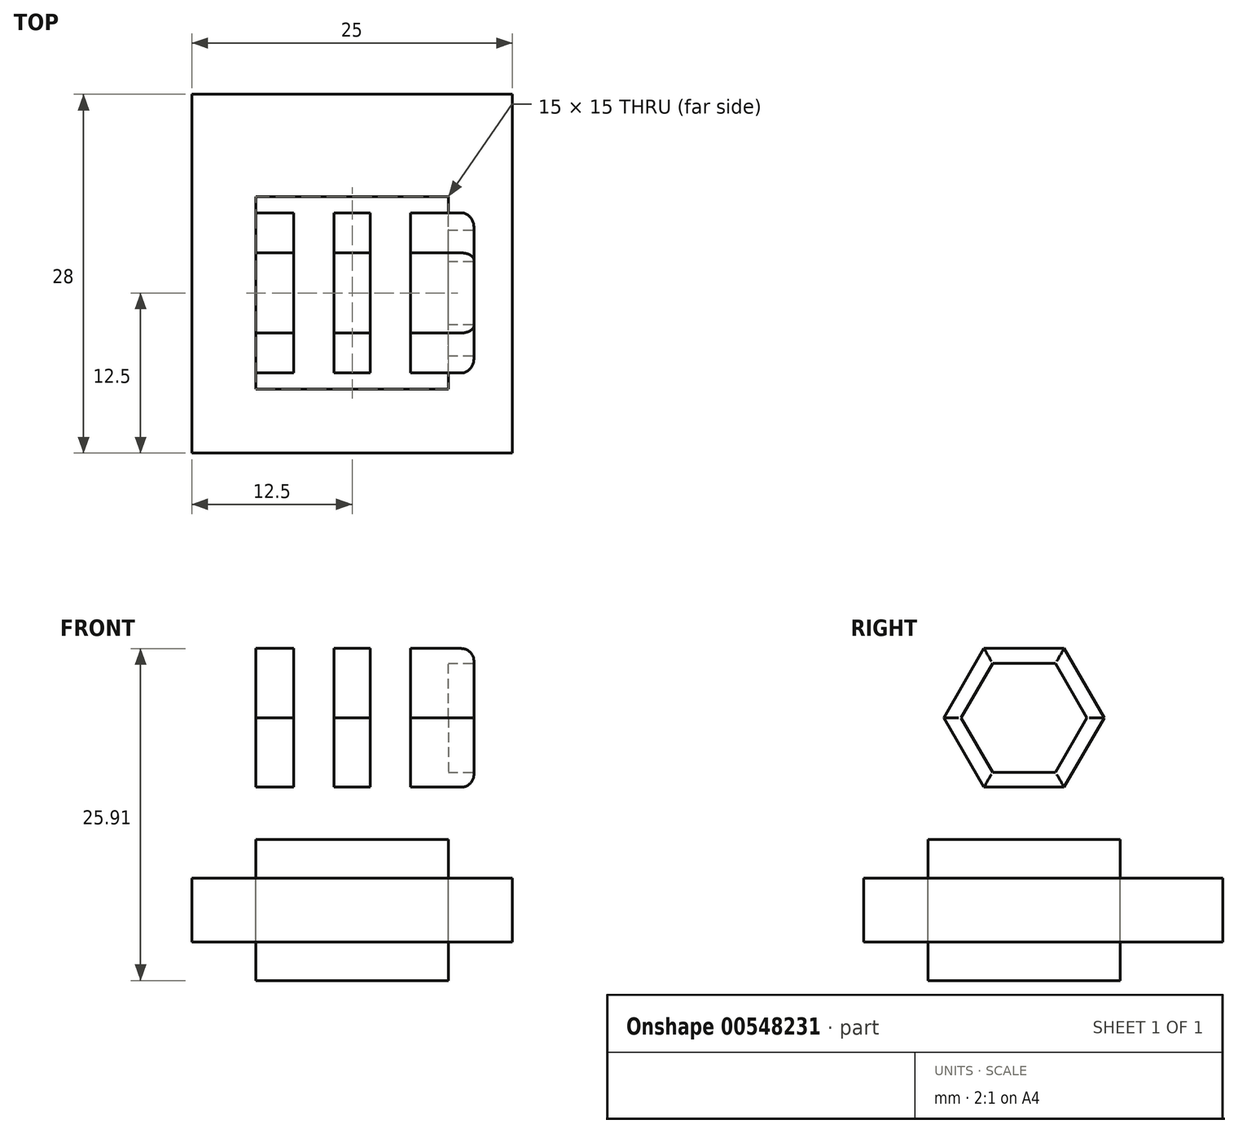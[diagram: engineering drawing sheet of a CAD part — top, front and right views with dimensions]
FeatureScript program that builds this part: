
annotation { "Feature Type Name" : "Feature", "Feature Type Description" : "" }
export const myFeature = defineFeature(function(context is Context, id is Id, definition is map)
    precondition{}
    {
        {
            var Q0;
            Q0=qCreatedBy(makeId("Right.planeOp"),FACE);
            var sketch = newSketch(context, id + "F0", { "sketchPlane" : qUnion([Q0])});
            skPoint(sketch, "E0", {"position": v(0, 12.5) * mm});
            skPoint(sketch, "E1", {"position": v(7.5, 0) * mm});
            skPoint(sketch, "E2.end.orphan", {"position": v(-7.5, 0) * mm});
            skLineSegment(sketch, "E3.top", {"start": v(-7.5, 0) * mm, "end": v(7.5, 0) * mm});
            skLineSegment(sketch, "E3.left", {"start": v(-7.5, 12.5) * mm, "end": v(-7.5, 0) * mm});
            skLineSegment(sketch, "E3.right", {"start": v(7.5, 12.5) * mm, "end": v(7.5, 0) * mm});
            skArc(sketch, "E4", {"start": v(7.5, 12.5) * mm, "mid": v(0, 20) * mm, "end": v(-7.5, 12.5) * mm});
            skCircle(sketch, "E5.cCircle", {"center": v(0, 12.5) * mm, "radius": 4.25 * mm, "construction": true});
            skLineSegment(sketch, "E5.0", {"start": v(-2.45, 16.75) * mm, "end": v(2.45, 16.75) * mm});
            skLineSegment(sketch, "E5.1", {"start": v(2.45, 16.75) * mm, "end": v(4.9, 12.5) * mm});
            skLineSegment(sketch, "E5.2", {"start": v(4.9, 12.5) * mm, "end": v(2.45, 8.25) * mm});
            skLineSegment(sketch, "E5.3", {"start": v(2.45, 8.25) * mm, "end": v(-2.45, 8.25) * mm});
            skLineSegment(sketch, "E5.4", {"start": v(-2.45, 8.25) * mm, "end": v(-4.9, 12.5) * mm});
            skLineSegment(sketch, "E5.5", {"start": v(-4.9, 12.5) * mm, "end": v(-2.45, 16.75) * mm});
            skPoint(sketch, "E5.0.midPoint", {"position": v(0, 16.75) * mm});
            skCircle(sketch, "E6.cCircle", {"center": v(0, 12.5) * mm, "radius": 5.41 * mm, "construction": true});
            skLineSegment(sketch, "E6.0", {"start": v(-3.12, 17.91) * mm, "end": v(3.12, 17.91) * mm});
            skLineSegment(sketch, "E6.1", {"start": v(3.12, 17.91) * mm, "end": v(6.25, 12.5) * mm});
            skLineSegment(sketch, "E6.2", {"start": v(6.25, 12.5) * mm, "end": v(3.12, 7.09) * mm});
            skLineSegment(sketch, "E6.3", {"start": v(3.13, 7.09) * mm, "end": v(-3.12, 7.09) * mm});
            skLineSegment(sketch, "E6.4", {"start": v(-3.12, 7.09) * mm, "end": v(-6.25, 12.5) * mm});
            skLineSegment(sketch, "E6.5", {"start": v(-6.25, 12.5) * mm, "end": v(-3.12, 17.91) * mm});
            skPoint(sketch, "E6.0.midPoint", {"position": v(0, 17.91) * mm});
            skLineSegment(sketch, "E7.top", {"start": v(-7.5, 3) * mm, "end": v(7.5, 3) * mm});
            skLineSegment(sketch, "E7.left", {"start": v(-7.5, 0) * mm, "end": v(-7.5, 3) * mm});
            skLineSegment(sketch, "E7.right", {"start": v(7.5, 0) * mm, "end": v(7.5, 3) * mm});
            skSolve(sketch);
        }
        {
            var Q0;
            Q0=makeQuery(id+"F0.imprint","IMPRINT",FACE,{"disambiguationData":[TD([[makeQuery(id+"F0.imprint","IMPRINT",EDGE,{"derivedFrom":sQuery(id+"F0.wireOp",EDGE,"E3.top")}),1.0]])]});
            extrude(context, id + "F1", {"entities" : qUnion([Q0]), "oppositeDirection" : true, "depth" : 15 * mm, "offsetDistance" : 25 * mm});
        }
        {
            var Q0;
            Q0=makeQuery(id+"F0.imprint","IMPRINT",FACE,{"disambiguationData":[TD([[makeQuery(id+"F0.imprint","IMPRINT",EDGE,{"derivedFrom":sQuery(id+"F0.wireOp",EDGE,"E3.left")}),1.0]])]});
            extrude(context, id + "F2", {"entities" : qUnion([Q0]), "operationType" : NewBodyOperationType.ADD, "oppositeDirection" : true, "depth" : 3 * mm});
        }
        {
            var Q0;
            Q0=makeQuery(id+"F0.imprint","IMPRINT",FACE,{"disambiguationData":[TD([[makeQuery(id+"F0.imprint","IMPRINT",EDGE,{"derivedFrom":sQuery(id+"F0.wireOp",EDGE,"E5.0")}),1.0]])]});
            extrude(context, id + "F3", {"entities" : qUnion([Q0]), "operationType" : NewBodyOperationType.ADD, "oppositeDirection" : true, "depth" : 3 * mm, "offsetDistance" : 25 * mm});
        }
        {
            var Q0;
            Q0=makeQuery(id+"F0.imprint","IMPRINT",FACE,{"disambiguationData":[TD([[makeQuery(id+"F0.imprint","IMPRINT",EDGE,{"derivedFrom":sQuery(id+"F0.wireOp",EDGE,"E5.0")}),1.0]])]});
            extrude(context, id + "F4", {"entities" : qUnion([Q0]), "operationType" : NewBodyOperationType.ADD, "depth" : 2 * mm, "offsetDistance" : 25 * mm});
        }
        {
            var Q0;
            Q0=makeQuery(id+"F0.imprint","IMPRINT",FACE,{"disambiguationData":[TD([[makeQuery(id+"F0.imprint","IMPRINT",EDGE,{"derivedFrom":sQuery(id+"F0.wireOp",EDGE,"E5.0")}),-1.0]])]});
            extrude(context, id + "F5", {"entities" : qUnion([Q0]), "operationType" : NewBodyOperationType.ADD, "oppositeDirection" : true, "depth" : 3 * mm});
        }
        {
            var Q0;
            {var subQ0=sQuery(id+"F0.wireOp",EDGE,"E5.5");var subQ1=sQuery(id+"F0.wireOp",EDGE,"E5.4");var subQ2=sQuery(id+"F0.wireOp",EDGE,"E5.3");var subQ3=sQuery(id+"F0.wireOp",EDGE,"E5.2");var subQ4=sQuery(id+"F0.wireOp",EDGE,"E5.1");var subQ5=sQuery(id+"F0.wireOp",EDGE,"E5.0");var subQ6=sQuery(id+"F0.wireOp",EDGE,"E6.5");var subQ7=sQuery(id+"F0.wireOp",EDGE,"E6.4");var subQ8=sQuery(id+"F0.wireOp",EDGE,"E6.3");var subQ9=sQuery(id+"F0.wireOp",EDGE,"E6.2");var subQ10=sQuery(id+"F0.wireOp",EDGE,"E6.1");var subQ11=sQuery(id+"F0.wireOp",EDGE,"E6.0");Q0=makeQuery(id+"F5.boolean.opBoolean","MERGE",FACE,{"derivedFrom":[makeQuery(id+"F3.boolean.opBoolean","MERGE",FACE,{"derivedFrom":[makeQuery(id+"F2.opExtrude","CAP_FACE",FACE,{"disambiguationData":[OSD([sQuery(id+"F0.wireOp",EDGE,"E3.left"),sQuery(id+"F0.wireOp",EDGE,"E3.right"),sQuery(id+"F0.wireOp",EDGE,"E4"),subQ11,subQ10,subQ9,subQ8,subQ7,subQ6,sQuery(id+"F0.wireOp",EDGE,"E7.top")])],"isStart":false}),makeQuery(id+"F3.opExtrude","CAP_FACE",FACE,{"disambiguationData":[OSD([subQ5,subQ4,subQ3,subQ2,subQ1,subQ0,subQ11,subQ10,subQ9,subQ8,subQ7,subQ6])],"isStart":false})]}),makeQuery(id+"F5.opExtrude","CAP_FACE",FACE,{"disambiguationData":[OSD([subQ5,subQ4,subQ3,subQ2,subQ1,subQ0])],"isStart":false})]});}
            extrude(context, id + "F6", {"entities" : qUnion([Q0]), "operationType" : NewBodyOperationType.ADD, "depth" : 12 * mm});
        }
        {
            var Q0;
            Q0=sQuery(id+"F0.wireOp",VERTEX,"E0");
            var Q1;
            Q1=makeQuery(id+"F1.opExtrude","SWEPT_BODY",BODY,{"disambiguationData":[OSD([sQuery(id+"F0.wireOp",EDGE,"E3.top"),sQuery(id+"F0.wireOp",EDGE,"E7.top"),sQuery(id+"F0.wireOp",EDGE,"E7.left"),sQuery(id+"F0.wireOp",EDGE,"E7.right")])]});
            hole(context, id + "F7", {"style" : HoleStyle.SIMPLE, "endStyle" : HoleEndStyle.BLIND, "holeDiameter" : 5 * mm, "holeDepth" : 15 * mm, "locations" : qUnion([Q0]), "scope" : qUnion([Q1])});
        }
        {
            var Q0;
            Q0=qCreatedBy(makeId("Top.planeOp"),FACE);
            cPlane(context, id + "F8", {"entities" : qUnion([Q0]), "cplaneType" : CPlaneType.OFFSET, "offset" : 20 * mm, "width" : 150 * mm, "height" : 150 * mm});
        }
        {
            var Q0;
            Q0=qCreatedBy(id+"F8.planeOp",FACE);
            var sketch = newSketch(context, id + "F9", { "sketchPlane" : qUnion([Q0])});
            skLineSegment(sketch, "E8.top", {"start": v(0, 7.5) * mm, "end": v(-15, 7.5) * mm});
            skLineSegment(sketch, "E8.left", {"start": v(0, 0) * mm, "end": v(0, 7.5) * mm});
            skLineSegment(sketch, "E8.right", {"start": v(-15, 0) * mm, "end": v(-15, 7.5) * mm});
            skLineSegment(sketch, "E9.top", {"start": v(-15, -7.5) * mm, "end": v(0, -7.5) * mm});
            skLineSegment(sketch, "E9.left", {"start": v(-15, 0) * mm, "end": v(-15, -7.5) * mm});
            skLineSegment(sketch, "E9.right", {"start": v(0, 0) * mm, "end": v(0, -7.5) * mm});
            skLineSegment(sketch, "E10", {"start": v(-7.5, -7.5) * mm, "end": v(-7.5, 7.5) * mm, "construction": true});
            skPoint(sketch, "E11", {"position": v(-6.1, -7.5) * mm});
            skLineSegment(sketch, "E12.bottom", {"start": v(-6.1, -7.5) * mm, "end": v(-8.9, -7.5) * mm});
            skLineSegment(sketch, "E12.top", {"start": v(-6.1, 7.5) * mm, "end": v(-8.9, 7.5) * mm});
            skLineSegment(sketch, "E12.left", {"start": v(-6.1, -7.5) * mm, "end": v(-6.1, 7.5) * mm});
            skLineSegment(sketch, "E12.right", {"start": v(-8.9, -7.5) * mm, "end": v(-8.9, 7.5) * mm});
            skLineSegment(sketch, "E13.bottom", {"start": v(-15, -7.5) * mm, "end": v(-12.05, -7.5) * mm});
            skLineSegment(sketch, "E13.top", {"start": v(-15, 7.5) * mm, "end": v(-12.05, 7.5) * mm});
            skLineSegment(sketch, "E13.left", {"start": v(-15, -7.5) * mm, "end": v(-15, 7.5) * mm});
            skLineSegment(sketch, "E13.right", {"start": v(-12.05, -7.5) * mm, "end": v(-12.05, 7.5) * mm});
            skLineSegment(sketch, "E14.bottom", {"start": v(0, -7.5) * mm, "end": v(-2.95, -7.5) * mm});
            skLineSegment(sketch, "E14.top", {"start": v(0, 7.5) * mm, "end": v(-2.95, 7.5) * mm});
            skLineSegment(sketch, "E14.left", {"start": v(0, -7.5) * mm, "end": v(0, 7.5) * mm});
            skLineSegment(sketch, "E14.right", {"start": v(-2.95, -7.5) * mm, "end": v(-2.95, 7.5) * mm});
            skSolve(sketch);
        }
        {
            var Q0;
            {var subQ2=sQuery(id+"F9.wireOp",EDGE,"E12.right");Q0=makeQuery(id+"F9.imprint","IMPRINT",FACE,{"disambiguationData":[TD([[makeQuery(id+"F9.imprint","IMPRINT",EDGE,{"derivedFrom":subQ2}),1.0]])]});}
            var Q1;
            {var subQ2=sQuery(id+"F9.wireOp",EDGE,"E12.left");Q1=makeQuery(id+"F9.imprint","IMPRINT",FACE,{"disambiguationData":[TD([[makeQuery(id+"F9.imprint","IMPRINT",EDGE,{"derivedFrom":subQ2}),-1.0]])]});}
            extrude(context, id + "F10", {"entities" : qUnion([Q0, Q1]), "operationType" : NewBodyOperationType.REMOVE, "oppositeDirection" : true, "depth" : 17 * mm});
        }
        {
            var Q0;
            Q0=makeQuery(id+"F4.opExtrude","CAP_EDGE",EDGE,{"disambiguationData":[OSD([sQuery(id+"F0.wireOp",EDGE,"E6.4")])],"isStart":false});
            var Q1;
            Q1=makeQuery(id+"F4.opExtrude","CAP_EDGE",EDGE,{"disambiguationData":[OSD([sQuery(id+"F0.wireOp",EDGE,"E6.3")])],"isStart":false});
            var Q2;
            Q2=makeQuery(id+"F4.opExtrude","CAP_EDGE",EDGE,{"disambiguationData":[OSD([sQuery(id+"F0.wireOp",EDGE,"E6.5")])],"isStart":false});
            var Q3;
            Q3=makeQuery(id+"F4.opExtrude","CAP_EDGE",EDGE,{"disambiguationData":[OSD([sQuery(id+"F0.wireOp",EDGE,"E6.0")])],"isStart":false});
            var Q4;
            Q4=makeQuery(id+"F4.opExtrude","CAP_EDGE",EDGE,{"disambiguationData":[OSD([sQuery(id+"F0.wireOp",EDGE,"E6.1")])],"isStart":false});
            var Q5;
            Q5=makeQuery(id+"F4.opExtrude","CAP_EDGE",EDGE,{"disambiguationData":[OSD([sQuery(id+"F0.wireOp",EDGE,"E6.2")])],"isStart":false});
            fillet(context, id + "F11", {"entities" : qUnion([Q0, Q1, Q2, Q3, Q4, Q5]), "radius" : 1 * mm, "tangentPropagation" : true, "allowEdgeOverflow" : false});
        }
        {
            var Q0;
            Q0=makeQuery(id+"F1.opExtrude","SWEPT_FACE",FACE,{"disambiguationData":[OSD([sQuery(id+"F0.wireOp",EDGE,"E3.top")])]});
            var sketch = newSketch(context, id + "F12", { "sketchPlane" : qUnion([Q0])});
            skLineSegment(sketch, "E15", {"start": v(0, 7.5) * mm, "end": v(-15, -7.5) * mm, "construction": true});
            skLineSegment(sketch, "E16", {"start": v(0, -7.5) * mm, "end": v(-15, 7.5) * mm, "construction": true});
            skPoint(sketch, "E17.middle", {"position": v(-7.5, 0) * mm});
            skLineSegment(sketch, "E18.bottom", {"start": v(-20, -15.5) * mm, "end": v(5, -15.5) * mm});
            skLineSegment(sketch, "E18.top", {"start": v(-20, 12.5) * mm, "end": v(5, 12.5) * mm});
            skLineSegment(sketch, "E18.left", {"start": v(-20, -15.5) * mm, "end": v(-20, 12.5) * mm});
            skLineSegment(sketch, "E18.right", {"start": v(5, -15.5) * mm, "end": v(5, 12.5) * mm});
            skPoint(sketch, "E18.middle", {"position": v(-7.5, -1.5) * mm});
            skLineSegment(sketch, "E19.bottom", {"start": v(-15, 7.5) * mm, "end": v(0, 7.5) * mm});
            skLineSegment(sketch, "E19.top", {"start": v(-15, -7.5) * mm, "end": v(0, -7.5) * mm});
            skLineSegment(sketch, "E19.left", {"start": v(-15, 7.5) * mm, "end": v(-15, -7.5) * mm});
            skLineSegment(sketch, "E19.right", {"start": v(0, 7.5) * mm, "end": v(0, -7.5) * mm});
            skLineSegment(sketch, "E20", {"start": v(-15, 7.5) * mm, "end": v(-15, 12.5) * mm, "construction": true});
            skLineSegment(sketch, "E21", {"start": v(-15, -7.5) * mm, "end": v(-20, -7.5) * mm, "construction": true});
            skSolve(sketch);
        }
        {
            var Q0;
            Q0 = qSketchRegion(id + "F12", true);
            extrude(context, id + "F13", {"entities" : qUnion([Q0]), "depth" : 5 * mm, "offsetDistance" : 25 * mm});
        }
        {
            var Q0;
            Q0=makeQuery(id+"F1.opExtrude","SWEPT_FACE",FACE,{"disambiguationData":[OSD([sQuery(id+"F0.wireOp",EDGE,"E3.top")])]});
            extrude(context, id + "F14", {"entities" : qUnion([Q0]), "depth" : 8 * mm, "offsetDistance" : 25 * mm});
        }
    });
